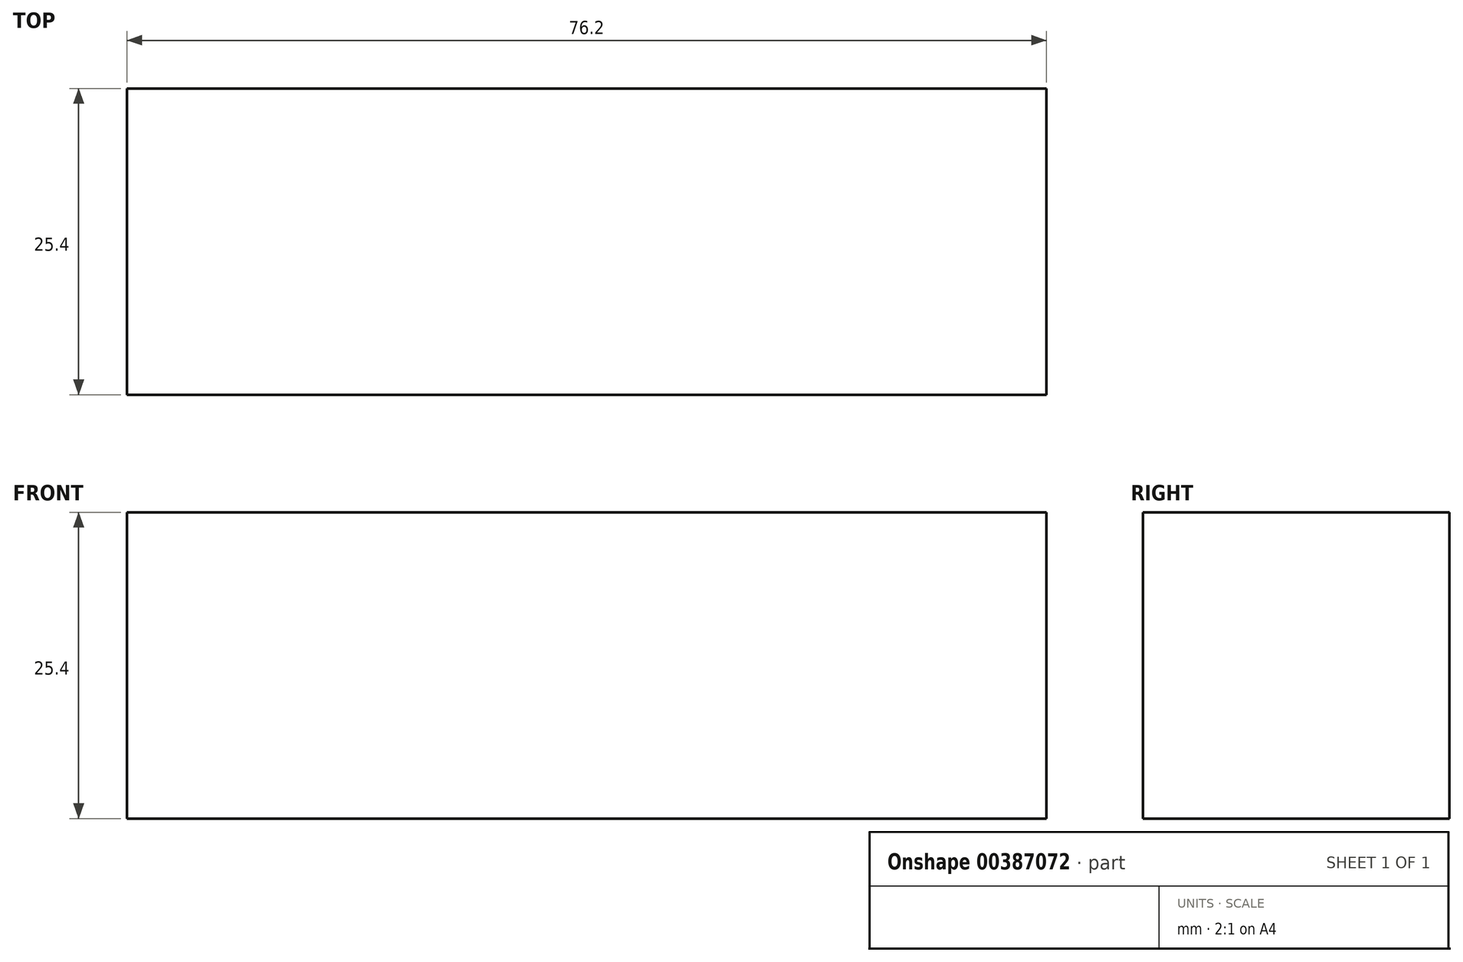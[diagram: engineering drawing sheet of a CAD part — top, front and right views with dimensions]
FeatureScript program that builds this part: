
annotation { "Feature Type Name" : "Feature", "Feature Type Description" : "" }
export const myFeature = defineFeature(function(context is Context, id is Id, definition is map)
    precondition{}
    {
        {
            var Q0;
            Q0=qCreatedBy(makeId("Front.planeOp"),FACE);
            var sketch = newSketch(context, id + "F0", { "sketchPlane" : qUnion([Q0])});
            skLineSegment(sketch, "E0.bottom", {"start": v(0, 0) * mm, "end": v(25.4, 0) * mm});
            skLineSegment(sketch, "E0.top", {"start": v(0, 25.4) * mm, "end": v(25.4, 25.4) * mm});
            skLineSegment(sketch, "E0.left", {"start": v(0, 0) * mm, "end": v(0, 25.4) * mm});
            skLineSegment(sketch, "E0.right", {"start": v(25.4, 0) * mm, "end": v(25.4, 25.4) * mm});
            skLineSegment(sketch, "E1.bottom", {"start": v(0, 25.4) * mm, "end": v(-25.4, 25.4) * mm});
            skLineSegment(sketch, "E1.top", {"start": v(0, 0) * mm, "end": v(-25.4, 0) * mm});
            skLineSegment(sketch, "E1.left", {"start": v(0, 25.4) * mm, "end": v(0, 0) * mm});
            skLineSegment(sketch, "E1.right", {"start": v(-25.4, 25.4) * mm, "end": v(-25.4, 0) * mm});
            skLineSegment(sketch, "E2.bottom", {"start": v(-25.4, 25.4) * mm, "end": v(0, 25.4) * mm});
            skLineSegment(sketch, "E2.top", {"start": v(-25.4, 49.4) * mm, "end": v(0, 49.4) * mm});
            skLineSegment(sketch, "E2.left", {"start": v(-25.4, 25.4) * mm, "end": v(-25.4, 49.4) * mm});
            skLineSegment(sketch, "E2.right", {"start": v(0, 25.4) * mm, "end": v(0, 49.4) * mm});
            skLineSegment(sketch, "E3.bottom", {"start": v(-25.4, 25.4) * mm, "end": v(-50.8, 25.4) * mm});
            skLineSegment(sketch, "E3.top", {"start": v(-25.4, 0) * mm, "end": v(-50.8, 0) * mm});
            skLineSegment(sketch, "E3.right", {"start": v(-50.8, 25.4) * mm, "end": v(-50.8, 0) * mm});
            skSolve(sketch);
        }
        {
            var Q0;
            Q0=makeQuery(id+"F0.imprint","IMPRINT",FACE,{"disambiguationData":[TD([[makeQuery(id+"F0.imprint","IMPRINT",EDGE,{"derivedFrom":sQuery(id+"F0.wireOp",EDGE,"E3.bottom")}),1.0]])]});
            var Q1;
            Q1=makeQuery(id+"F0.imprint","IMPRINT",FACE,{"disambiguationData":[TD([[makeQuery(id+"F0.imprint","IMPRINT",EDGE,{"derivedFrom":sQuery(id+"F0.wireOp",EDGE,"E2.bottom")}),1.0]])]});
            var Q2;
            Q2=makeQuery(id+"F0.imprint","IMPRINT",FACE,{"disambiguationData":[TD([[makeQuery(id+"F0.imprint","IMPRINT",EDGE,{"derivedFrom":sQuery(id+"F0.wireOp",EDGE,"E1.top")}),-1.0]])]});
            var Q3;
            Q3=makeQuery(id+"F0.imprint","IMPRINT",FACE,{"disambiguationData":[TD([[makeQuery(id+"F0.imprint","IMPRINT",EDGE,{"derivedFrom":sQuery(id+"F0.wireOp",EDGE,"E0.bottom")}),1.0]])]});
            extrude(context, id + "F1", {"entities" : qUnion([Q0, Q1, Q2, Q3]), "depth" : 25.4 * mm});
        }
    });
